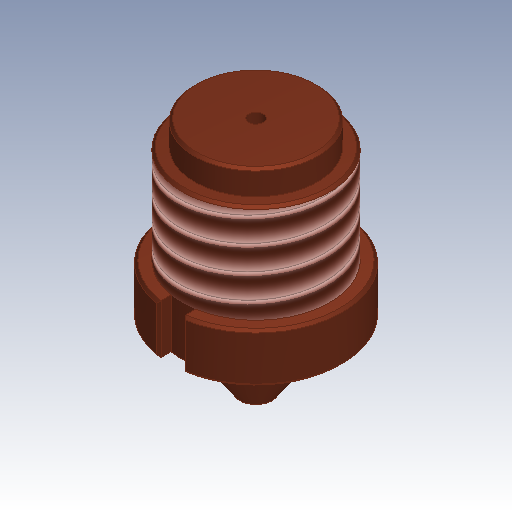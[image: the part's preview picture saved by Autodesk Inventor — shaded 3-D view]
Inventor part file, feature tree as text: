
AUTODESK INVENTOR PART (.ipt)
format: ipt  version: 2023.3 (Build 273359000, 359)  size: 271,360 bytes
history: native  units: in
note: dims shown in document units (in); Inventor stores cm internally (conversion verified against a paired STEP export)
features: chamfer x3, sketch x2, revolve x1, fillet x1, thread x1, extrude x1, pattern_circular x1
ambient origin geometry x8: Origin, YZ Plane, XZ Plane, XY Plane, X Axis, Y Axis, Z Axis, Center Point
bodies: Body1 (feature_tree)
feature tree (10):
  revolve  "Umdrehung1"
  chamfer  "Fase1"  Distance=0.0236in
  fillet  "Rundung2"  Radius=0.0472in
  chamfer  "Fase2"  Distance=0.1969in
  thread  "Gewinde1"  [1 undecoded]
  extrude  "Extrusion3"  Depth=0.2362in
  chamfer  "Fase3"  Distance=0.1969in
  pattern_circular  "Runde Anordnung1"  Angle=90.0deg  [1 undecoded]
  sketch  "Skizze3"  dims[d6=0.0787in]
  sketch  "Skizze4"  dims[d7=0.2756in d10=0.0236in d12=0.0472in d13=0.1969in d14=0.0394in d15=0.2362in d16=0.1969in d17=90.0deg d20=0.3779in d21=0.0039in d22=0.0787in d23=45.0deg d25=0.0079in d26=0.0079in d27=0.0787in d28=45.0deg d29=0.2362in d30=0.0in d31=0.0394in d32=0.0394in d33=0.0197in d34=0.0in d35=0.0in d36=0.0039in d37=0.0787in d38=45.0deg d39=0.7874in d40=360.0deg]
note: 2 required parameter values undecoded (feature->parameter linkage not recoverable at this tier; creation-order binding heuristic only, values carry confidence <= 0.55)
